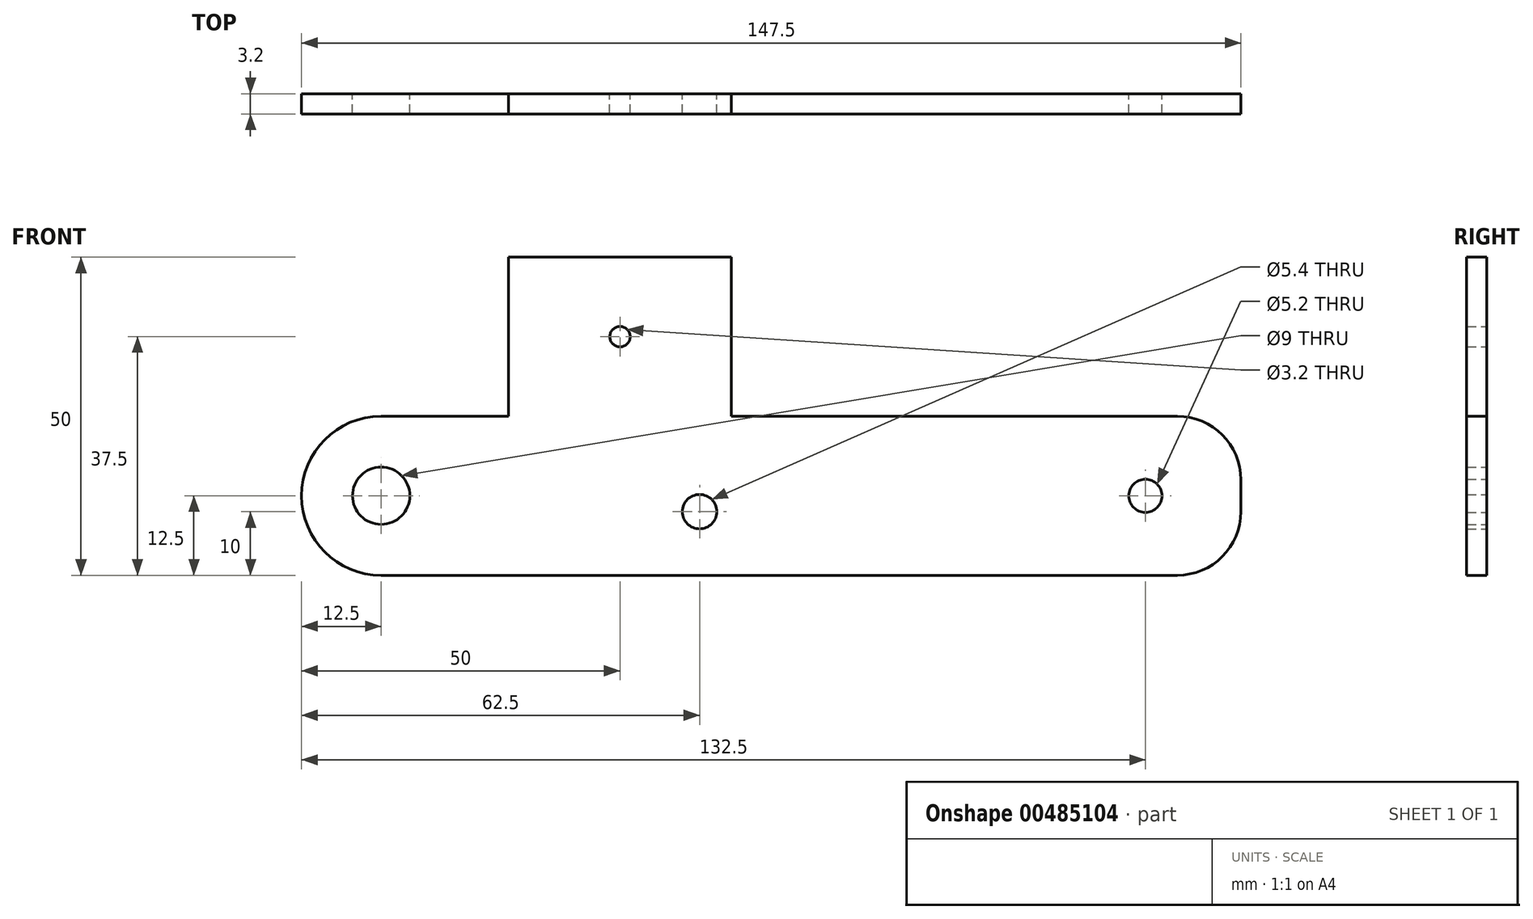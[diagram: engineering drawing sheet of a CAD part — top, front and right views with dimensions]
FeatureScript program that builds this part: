
annotation { "Feature Type Name" : "Feature", "Feature Type Description" : "" }
export const myFeature = defineFeature(function(context is Context, id is Id, definition is map)
    precondition{}
    {
        {
            var Q0;
            Q0=qCreatedBy(makeId("Front.planeOp"),FACE);
            var sketch = newSketch(context, id + "F0", { "sketchPlane" : qUnion([Q0])});
            skLineSegment(sketch, "E0.top", {"start": v(-75, -12.5) * mm, "end": v(75, -12.5) * mm, "construction": true});
            skLineSegment(sketch, "E0.left", {"start": v(-75, 12.5) * mm, "end": v(-75, -12.5) * mm, "construction": true});
            skLineSegment(sketch, "E0.right", {"start": v(75, 12.5) * mm, "end": v(75, -12.5) * mm});
            skPoint(sketch, "E0.middle", {"position": v(0, 0) * mm});
            skLineSegment(sketch, "E1", {"start": v(-40, 12.5) * mm, "end": v(-40, -12.5) * mm, "construction": true});
            skLineSegment(sketch, "E2", {"start": v(45, 12.5) * mm, "end": v(45, -12.5) * mm, "construction": true});
            skLineSegment(sketch, "E3", {"start": v(-60, 12.5) * mm, "end": v(-60, -12.5) * mm, "construction": true});
            skLineSegment(sketch, "E4", {"start": v(60, 23.8) * mm, "end": v(60, -12.5) * mm, "construction": true});
            skLineSegment(sketch, "E5", {"start": v(-75, 0) * mm, "end": v(75, 0) * mm, "construction": true});
            skCircle(sketch, "E6", {"center": v(-60, 0) * mm, "radius": 4.5 * mm});
            skCircle(sketch, "E7", {"center": v(60, 0) * mm, "radius": 2.6 * mm});
            skArc(sketch, "E8", {"start": v(-60, -12.5) * mm, "mid": v(-72.5, 0) * mm, "end": v(-60, 12.5) * mm});
            skLineSegment(sketch, "E9", {"start": v(-60, -12.5) * mm, "end": v(75, -12.5) * mm});
            skLineSegment(sketch, "E10", {"start": v(-10, 15) * mm, "end": v(-10, -12.5) * mm, "construction": true});
            skLineSegment(sketch, "E11", {"start": v(75, -2.5) * mm, "end": v(-10, -2.5) * mm, "construction": true});
            skCircle(sketch, "E12", {"center": v(-10, -2.5) * mm, "radius": 2.7 * mm});
            skLineSegment(sketch, "E13", {"start": v(-5, 37.5) * mm, "end": v(-5, 12.5) * mm, "construction": true});
            skLineSegment(sketch, "E14", {"start": v(-5, 12.5) * mm, "end": v(-5, -12.5) * mm, "construction": true});
            skLineSegment(sketch, "E15", {"start": v(-5, 37.5) * mm, "end": v(-5, 12.5) * mm});
            skLineSegment(sketch, "E16", {"start": v(75, 12.5) * mm, "end": v(-5, 12.5) * mm});
            skLineSegment(sketch, "E17", {"start": v(-40, 25) * mm, "end": v(-5, 25) * mm, "construction": true});
            skLineSegment(sketch, "E18", {"start": v(-22.5, 37.5) * mm, "end": v(-22.5, 12.5) * mm, "construction": true});
            skPoint(sketch, "E18.endSnap0", {"position": v(-22.5, 25) * mm});
            skCircle(sketch, "E19", {"center": v(-22.5, 25) * mm, "radius": 1.6 * mm});
            skLineSegment(sketch, "E20", {"start": v(-5, 37.5) * mm, "end": v(-40, 37.5) * mm, "construction": true});
            skLineSegment(sketch, "E21", {"start": v(-40, 37.5) * mm, "end": v(-40, 12.5) * mm, "construction": true});
            skLineSegment(sketch, "E22", {"start": v(-75, 12.5) * mm, "end": v(75, 12.5) * mm, "construction": true});
            skLineSegment(sketch, "E23", {"start": v(-60, 12.5) * mm, "end": v(-40, 12.5) * mm});
            skLineSegment(sketch, "E24", {"start": v(-40, 37.5) * mm, "end": v(-5, 37.5) * mm});
            skLineSegment(sketch, "E25", {"start": v(-40, 12.5) * mm, "end": v(-40, 37.5) * mm});
            skSolve(sketch);
        }
        {
            var Q0;
            Q0=qSketchRegion(id+"F0",true);
            extrude(context, id + "F1", {"entities" : qUnion([Q0]), "depth" : 3.2 * mm});
        }
        {
            var Q0;
            Q0=makeQuery(id+"F1.opExtrude","SWEPT_EDGE",EDGE,{"disambiguationData":[OSD([sQuery(id+"F0.wireOp",EDGE,"E0.right"),sQuery(id+"F0.wireOp",EDGE,"E16")])]});
            var Q1;
            Q1=makeQuery(id+"F1.opExtrude","SWEPT_EDGE",EDGE,{"disambiguationData":[OSD([sQuery(id+"F0.wireOp",EDGE,"E0.right"),sQuery(id+"F0.wireOp",EDGE,"E9")])]});
            fillet(context, id + "F2", {"entities" : qUnion([Q0, Q1]), "radius" : 10 * mm, "tangentPropagation" : true, "allowEdgeOverflow" : false});
        }
    });
